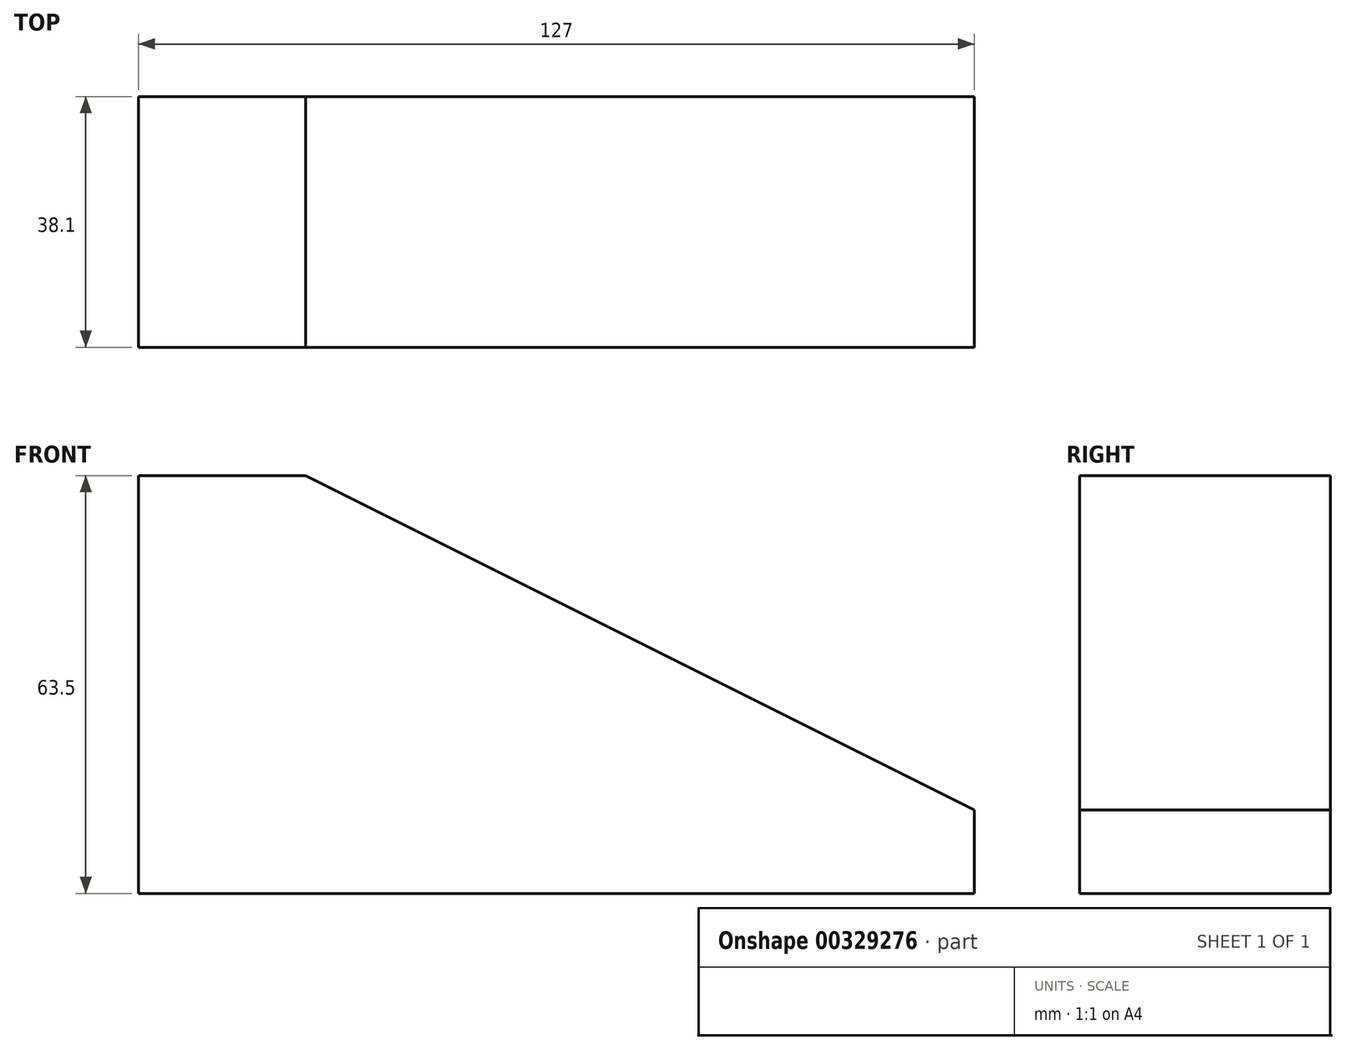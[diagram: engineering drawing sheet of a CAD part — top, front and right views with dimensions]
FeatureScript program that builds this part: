
annotation { "Feature Type Name" : "Feature", "Feature Type Description" : "" }
export const myFeature = defineFeature(function(context is Context, id is Id, definition is map)
    precondition{}
    {
        {
            var Q0;
            Q0=qCreatedBy(makeId("Front.planeOp"),FACE);
            var sketch = newSketch(context, id + "F0", { "sketchPlane" : qUnion([Q0])});
            skLineSegment(sketch, "E0", {"start": v(-56.91, -21.42) * mm, "end": v(70.09, -21.42) * mm});
            skLineSegment(sketch, "E1", {"start": v(-56.91, -21.42) * mm, "end": v(-56.91, 42.08) * mm});
            skLineSegment(sketch, "E2", {"start": v(-56.91, 42.08) * mm, "end": v(-31.51, 42.08) * mm});
            skLineSegment(sketch, "E3", {"start": v(70.09, -21.42) * mm, "end": v(70.09, -8.72) * mm});
            skLineSegment(sketch, "E4", {"start": v(-31.51, 42.08) * mm, "end": v(70.09, -8.72) * mm});
            skSolve(sketch);
        }
        {
            var Q0;
            Q0 = qSketchRegion(id + "F0", true);
            extrude(context, id + "F1", {"entities" : qUnion([Q0]), "depth" : 38.1 * mm});
        }
    });
